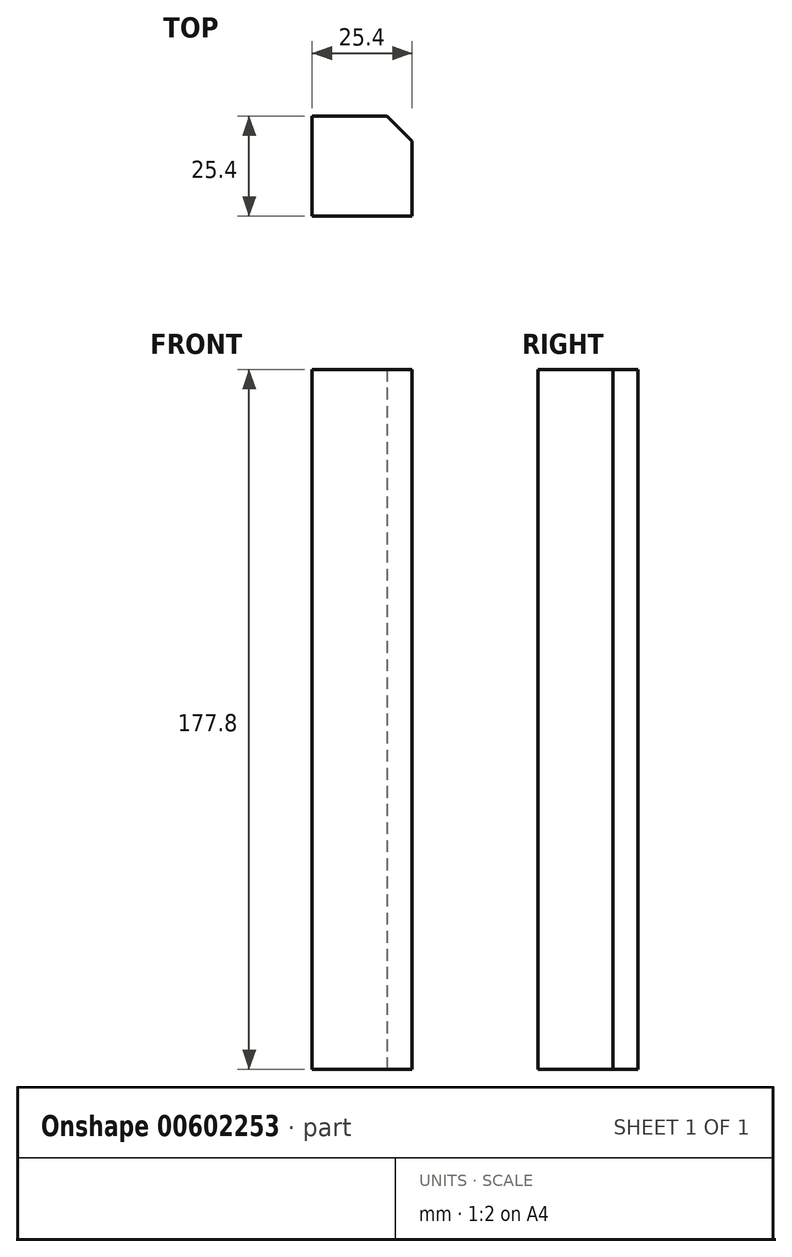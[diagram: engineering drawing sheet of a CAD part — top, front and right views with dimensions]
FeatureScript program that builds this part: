
annotation { "Feature Type Name" : "Feature", "Feature Type Description" : "" }
export const myFeature = defineFeature(function(context is Context, id is Id, definition is map)
    precondition{}
    {
        {
            var Q0;
            Q0=qCreatedBy(makeId("Top.planeOp"),FACE);
            var sketch = newSketch(context, id + "F0", { "sketchPlane" : qUnion([Q0])});
            skLineSegment(sketch, "E0.bottom", {"start": v(0, 0) * mm, "end": v(25.4, 0) * mm});
            skLineSegment(sketch, "E0.top", {"start": v(0, 25.4) * mm, "end": v(25.4, 25.4) * mm});
            skLineSegment(sketch, "E0.left", {"start": v(0, 0) * mm, "end": v(0, 25.4) * mm});
            skLineSegment(sketch, "E0.right", {"start": v(25.4, 0) * mm, "end": v(25.4, 25.4) * mm});
            skSolve(sketch);
        }
        {
            var Q0;
            Q0 = qSketchRegion(id + "F0", true);
            extrude(context, id + "F1", {"entities" : qUnion([Q0]), "depth" : 177.8 * mm, "offsetDistance" : 25.4 * mm});
        }
        {
            var Q0;
            Q0=makeQuery(id+"F1.opExtrude","SWEPT_EDGE",EDGE,{"disambiguationData":[OSD([sQuery(id+"F0.wireOp",EDGE,"E0.top"),sQuery(id+"F0.wireOp",EDGE,"E0.right")])]});
            chamfer(context, id + "F2", {"entities" : qUnion([Q0]), "chamferType" : ChamferType.OFFSET_ANGLE, "width" : 6.35 * mm, "oppositeDirection" : false, "angle" : 45 * degree, "tangentPropagation" : true});
        }
    });
